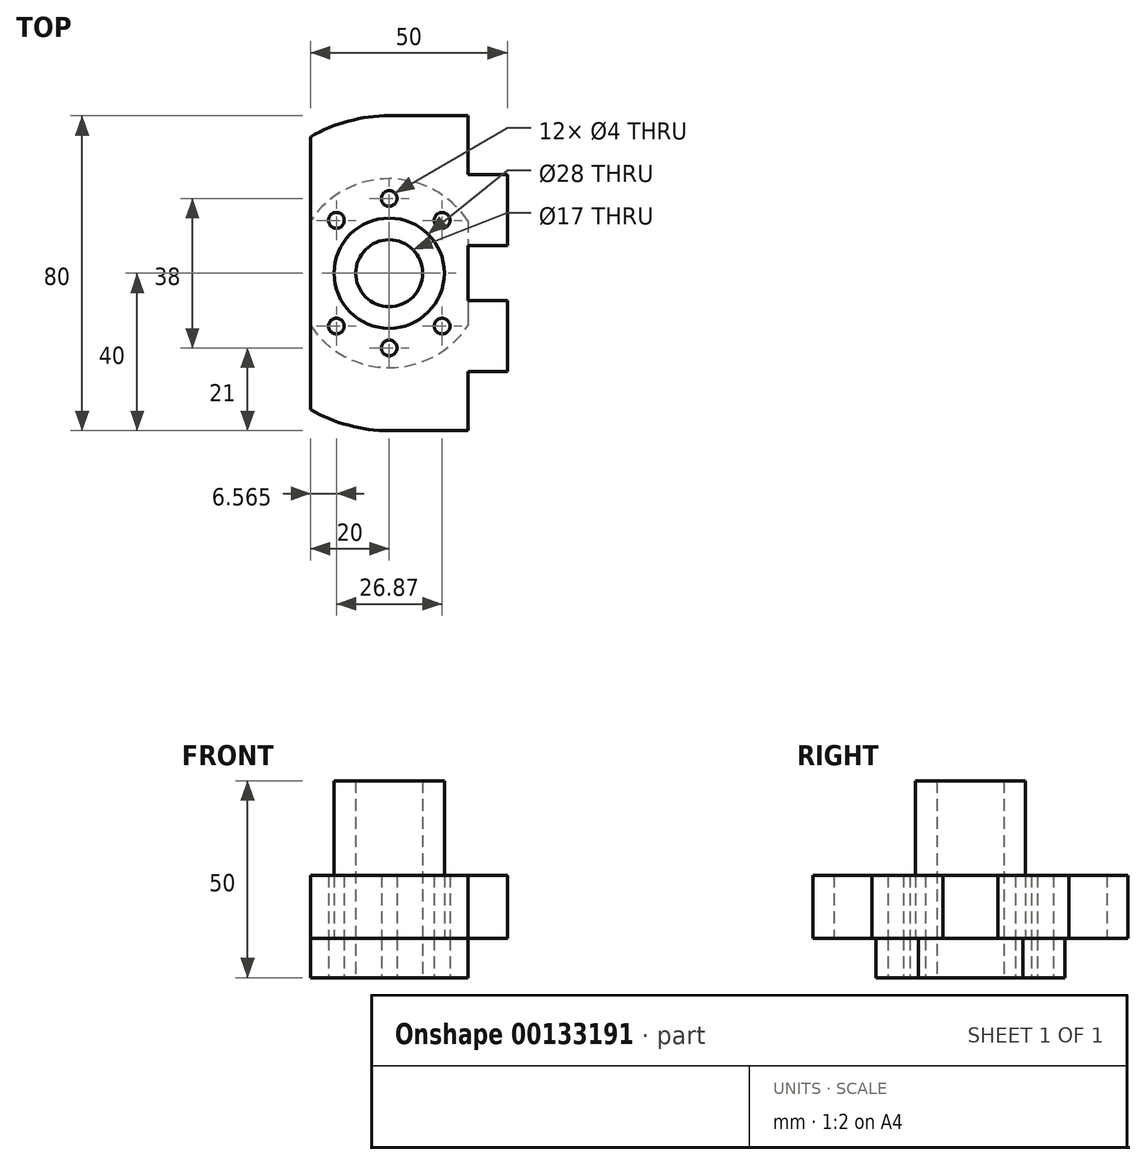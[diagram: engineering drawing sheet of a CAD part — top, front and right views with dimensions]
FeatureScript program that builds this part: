
annotation { "Feature Type Name" : "Feature", "Feature Type Description" : "" }
export const myFeature = defineFeature(function(context is Context, id is Id, definition is map)
    precondition{}
    {
        {
            var Q0;
            Q0=qCreatedBy(makeId("Top.planeOp"),FACE);
            var sketch = newSketch(context, id + "F0", { "sketchPlane" : qUnion([Q0])});
            skLineSegment(sketch, "E0", {"start": v(-20, 13.27) * mm, "end": v(-20, -13.27) * mm});
            skLineSegment(sketch, "E1", {"start": v(20, 13.27) * mm, "end": v(20, -13.27) * mm});
            skArc(sketch, "E2", {"start": v(-20, -13.27) * mm, "mid": v(0, -24) * mm, "end": v(20, -13.27) * mm});
            skArc(sketch, "E3.trimOffspring", {"start": v(20, 13.27) * mm, "mid": v(0, 24) * mm, "end": v(-20, 13.27) * mm});
            skCircle(sketch, "E4", {"center": v(0, 0) * mm, "radius": 8.5 * mm});
            skLineSegment(sketch, "E5", {"start": v(-13.44, 13.44) * mm, "end": v(0, 0) * mm, "construction": true});
            skLineSegment(sketch, "E6", {"start": v(0, 0) * mm, "end": v(0, 19) * mm, "construction": true});
            skLineSegment(sketch, "E7", {"start": v(0, 0) * mm, "end": v(13.44, 13.44) * mm, "construction": true});
            skLineSegment(sketch, "E8", {"start": v(0, 0) * mm, "end": v(-13.44, -13.44) * mm, "construction": true});
            skLineSegment(sketch, "E9", {"start": v(0, 0) * mm, "end": v(0, -19) * mm, "construction": true});
            skLineSegment(sketch, "E10", {"start": v(0, 0) * mm, "end": v(13.44, -13.44) * mm, "construction": true});
            skCircle(sketch, "E11", {"center": v(-13.44, 13.44) * mm, "radius": 2 * mm});
            skCircle(sketch, "E12", {"center": v(0, 19) * mm, "radius": 2 * mm});
            skCircle(sketch, "E13", {"center": v(13.44, 13.44) * mm, "radius": 2 * mm});
            skCircle(sketch, "E14", {"center": v(13.44, -13.44) * mm, "radius": 2 * mm});
            skCircle(sketch, "E15", {"center": v(0, -19) * mm, "radius": 2 * mm});
            skCircle(sketch, "E16", {"center": v(-13.44, -13.44) * mm, "radius": 2 * mm});
            skSolve(sketch);
        }
        {
            var Q0;
            Q0=qSketchRegion(id+"F0",true);
            extrude(context, id + "F1", {"entities" : qUnion([Q0]), "depth" : 10 * mm});
        }
        {
            var Q0;
            Q0=qCreatedBy(makeId("Right.planeOp"),FACE);
            var sketch = newSketch(context, id + "F2", { "sketchPlane" : qUnion([Q0])});
            skLineSegment(sketch, "E17.bottom", {"start": v(-14, 50) * mm, "end": v(-8.5, 50) * mm});
            skLineSegment(sketch, "E17.top", {"start": v(-14, 10) * mm, "end": v(-8.5, 10) * mm});
            skLineSegment(sketch, "E17.left", {"start": v(-14, 50) * mm, "end": v(-14, 10) * mm});
            skLineSegment(sketch, "E17.right", {"start": v(-8.5, 50) * mm, "end": v(-8.5, 10) * mm});
            skLineSegment(sketch, "E18", {"start": v(0, 0) * mm, "end": v(0, 60.4) * mm, "construction": true});
            skSolve(sketch);
        }
        {
            var Q0;
            Q0=qSketchRegion(id+"F2",true);
            var Q1;
            Q1=sQuery(id+"F2.wireOp",EDGE,"E18");
            revolve(context, id + "F3", {"operationType" : NewBodyOperationType.ADD, "entities" : qUnion([Q0]), "axis" : qUnion([Q1]), "revolveType" : RevolveType.FULL});
        }
        {
            var Q0;
            Q0=makeQuery(id+"F1.opExtrude","CAP_FACE",FACE,{"disambiguationData":[OSD([sQuery(id+"F0.wireOp",EDGE,"E0"),sQuery(id+"F0.wireOp",EDGE,"E1"),sQuery(id+"F0.wireOp",EDGE,"E2"),sQuery(id+"F0.wireOp",EDGE,"E3.trimOffspring"),sQuery(id+"F0.wireOp",EDGE,"E4"),sQuery(id+"F0.wireOp",EDGE,"E11"),sQuery(id+"F0.wireOp",EDGE,"E12"),sQuery(id+"F0.wireOp",EDGE,"E13"),sQuery(id+"F0.wireOp",EDGE,"E14"),sQuery(id+"F0.wireOp",EDGE,"E15"),sQuery(id+"F0.wireOp",EDGE,"E16")])],"isStart":false});
            var sketch = newSketch(context, id + "F4", { "sketchPlane" : qUnion([Q0])});
            skArc(sketch, "E19", {"start": v(0, 40) * mm, "mid": v(-10.35, 38.64) * mm, "end": v(-20, 34.64) * mm});
            skLineSegment(sketch, "E20", {"start": v(0, -40) * mm, "end": v(20, -40) * mm});
            skLineSegment(sketch, "E21", {"start": v(0, 40) * mm, "end": v(20, 40) * mm});
            skLineSegment(sketch, "E22", {"start": v(20, 40) * mm, "end": v(20, 25) * mm});
            skLineSegment(sketch, "E23.bottom", {"start": v(20, 25) * mm, "end": v(30, 25) * mm});
            skLineSegment(sketch, "E23.top", {"start": v(20, 7) * mm, "end": v(30, 7) * mm});
            skLineSegment(sketch, "E23.right", {"start": v(30, 25) * mm, "end": v(30, 7) * mm});
            skLineSegment(sketch, "E24.trimOffspring", {"start": v(20, 7) * mm, "end": v(20, 0) * mm});
            skLineSegment(sketch, "E25.MirrorCS", {"start": v(20, -7) * mm, "end": v(20, 0) * mm});
            skLineSegment(sketch, "E26.MirrorCS", {"start": v(30, -25) * mm, "end": v(30, -7) * mm});
            skLineSegment(sketch, "E27.MirrorCS", {"start": v(20, -40) * mm, "end": v(20, -25) * mm});
            skLineSegment(sketch, "E28.MirrorCS", {"start": v(20, -7) * mm, "end": v(30, -7) * mm});
            skLineSegment(sketch, "E29.MirrorCS", {"start": v(20, -25) * mm, "end": v(30, -25) * mm});
            skLineSegment(sketch, "E30", {"start": v(-20, 34.64) * mm, "end": v(-20, -34.64) * mm});
            skArc(sketch, "E31.trimOffspring", {"start": v(-20, -34.64) * mm, "mid": v(-10.35, -38.64) * mm, "end": v(0, -40) * mm});
            skSolve(sketch);
        }
        {
            var Q0;
            Q0=makeQuery(id+"F4.imprint","IMPRINT",FACE,{"disambiguationData":[TD([[makeQuery(id+"F4.imprint","IMPRINT",EDGE,{"derivedFrom":sQuery(id+"F4.wireOp",EDGE,"E19")}),1.0]])]});
            var Q1;
            Q1=makeQuery(id+"F4.imprint","IMPRINT",FACE,{"disambiguationData":[TD([[makeQuery(id+"F4.imprint","IMPRINT",EDGE,{"derivedFrom":makeQuery(id+"F1.opExtrude","CAP_EDGE",EDGE,{"disambiguationData":[OSD([sQuery(id+"F0.wireOp",EDGE,"E0")])],"isStart":false})}),1.0]])]});
            var Q2;
            {var subQ1=sQuery(id+"F4.wireOp",EDGE,"E24.trimOffspring");Q2=makeQuery(id+"F4.imprint","IMPRINT",FACE,{"disambiguationData":[TD([[makeQuery(id+"F4.imprint","IMPRINT",EDGE,{"derivedFrom":subQ1}),-1.0]])]});}
            var Q3;
            Q3=makeQuery(id+"F4.imprint","IMPRINT",FACE,{"disambiguationData":[TD([[makeQuery(id+"F4.imprint","IMPRINT",EDGE,{"derivedFrom":sQuery(id+"F4.wireOp",EDGE,"E20")}),1.0]])]});
            extrude(context, id + "F5", {"entities" : qUnion([Q0, Q1, Q2, Q3]), "depth" : 16 * mm});
        }
    });
